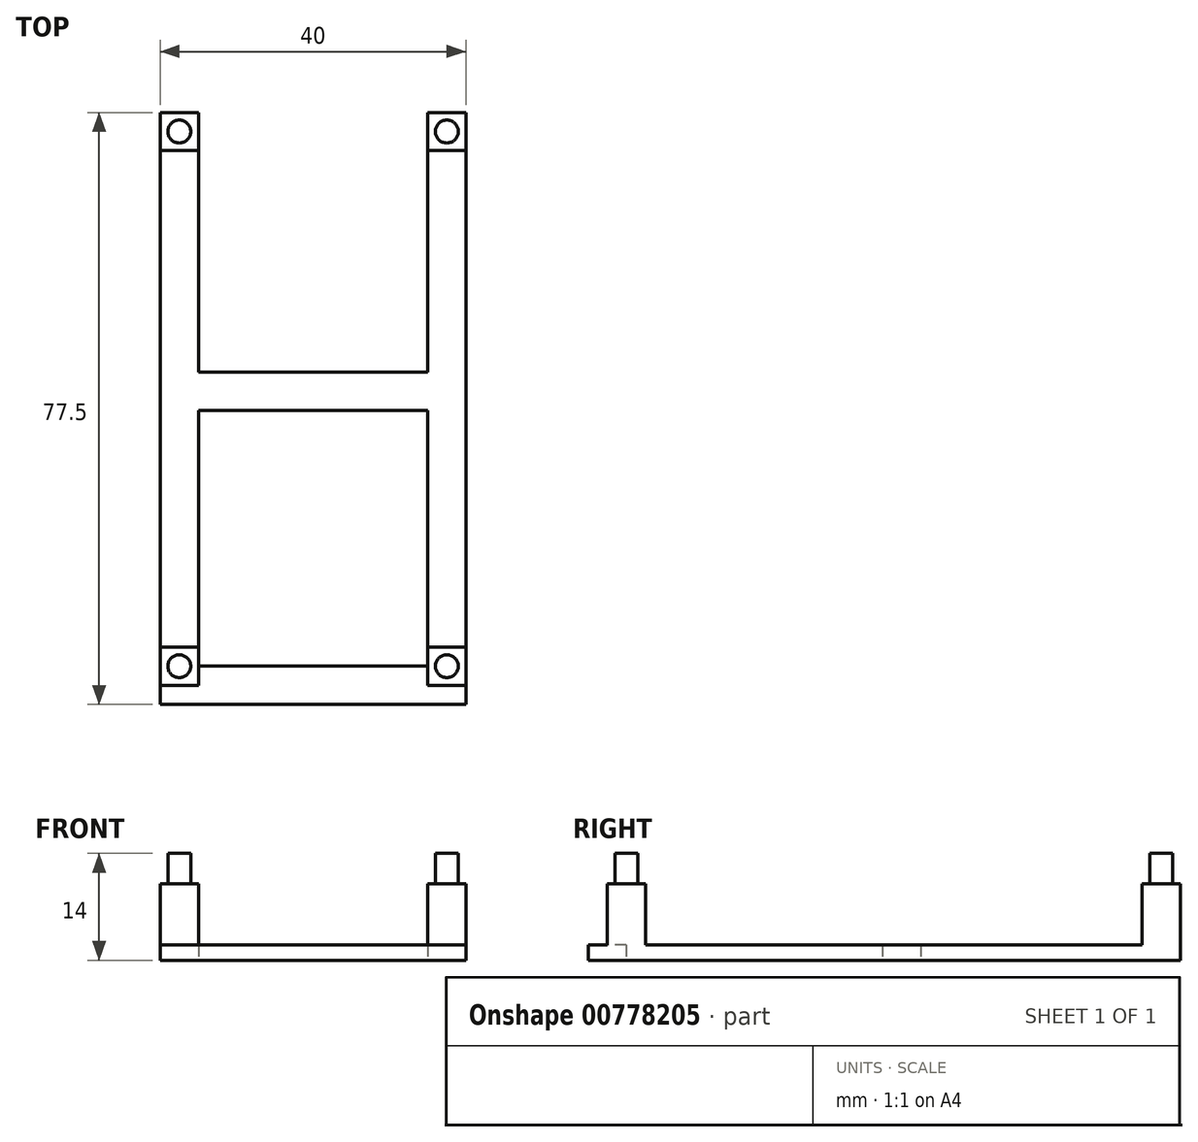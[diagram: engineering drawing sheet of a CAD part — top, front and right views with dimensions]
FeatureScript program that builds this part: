
annotation { "Feature Type Name" : "Feature", "Feature Type Description" : "" }
export const myFeature = defineFeature(function(context is Context, id is Id, definition is map)
    precondition{}
    {
        {
            var Q0;
            Q0=qCreatedBy(makeId("Top.planeOp"),FACE);
            var sketch = newSketch(context, id + "F0", { "sketchPlane" : qUnion([Q0])});
            skLineSegment(sketch, "E0.bottom", {"start": v(20, -41) * mm, "end": v(-20, -41) * mm});
            skLineSegment(sketch, "E0.top", {"start": v(20, 41) * mm, "end": v(-20, 41) * mm});
            skLineSegment(sketch, "E0.left", {"start": v(20, -41) * mm, "end": v(20, 41) * mm});
            skLineSegment(sketch, "E0.right", {"start": v(-20, -41) * mm, "end": v(-20, 41) * mm});
            skPoint(sketch, "E0.middle", {"position": v(0, 0) * mm});
            skLineSegment(sketch, "E1.bottom", {"start": v(-15, 31.5) * mm, "end": v(-20, 31.5) * mm});
            skLineSegment(sketch, "E1.top", {"start": v(-15, 36.5) * mm, "end": v(-20, 36.5) * mm});
            skLineSegment(sketch, "E1.left", {"start": v(-15, 31.5) * mm, "end": v(-15, 36.5) * mm});
            skLineSegment(sketch, "E1.right", {"start": v(-20, 31.5) * mm, "end": v(-20, 36.5) * mm});
            skPoint(sketch, "E1.middle", {"position": v(-17.5, 34) * mm});
            skCircle(sketch, "E2", {"center": v(-17.5, 34) * mm, "radius": 1.5 * mm});
            skLineSegment(sketch, "E3.bottom", {"start": v(20, 31.5) * mm, "end": v(15, 31.5) * mm});
            skLineSegment(sketch, "E3.top", {"start": v(20, 36.5) * mm, "end": v(15, 36.5) * mm});
            skLineSegment(sketch, "E3.left", {"start": v(20, 31.5) * mm, "end": v(20, 36.5) * mm});
            skLineSegment(sketch, "E3.right", {"start": v(15, 31.5) * mm, "end": v(15, 36.5) * mm});
            skPoint(sketch, "E3.middle", {"position": v(17.5, 34) * mm});
            skLineSegment(sketch, "E4.bottom", {"start": v(20, -38.5) * mm, "end": v(15, -38.5) * mm});
            skLineSegment(sketch, "E4.top", {"start": v(20, -33.5) * mm, "end": v(15, -33.5) * mm});
            skLineSegment(sketch, "E4.left", {"start": v(20, -38.5) * mm, "end": v(20, -33.5) * mm});
            skLineSegment(sketch, "E4.right", {"start": v(15, -38.5) * mm, "end": v(15, -33.5) * mm});
            skPoint(sketch, "E4.middle", {"position": v(17.5, -36) * mm});
            skLineSegment(sketch, "E5.bottom", {"start": v(-15, -38.5) * mm, "end": v(-20, -38.5) * mm});
            skLineSegment(sketch, "E5.top", {"start": v(-15, -33.5) * mm, "end": v(-20, -33.5) * mm});
            skLineSegment(sketch, "E5.left", {"start": v(-15, -38.5) * mm, "end": v(-15, -33.5) * mm});
            skLineSegment(sketch, "E5.right", {"start": v(-20, -38.5) * mm, "end": v(-20, -33.5) * mm});
            skPoint(sketch, "E5.middle", {"position": v(-17.5, -36) * mm});
            skCircle(sketch, "E6", {"center": v(17.5, 34) * mm, "radius": 1.5 * mm});
            skCircle(sketch, "E7", {"center": v(-17.5, -36) * mm, "radius": 1.5 * mm});
            skCircle(sketch, "E8", {"center": v(17.5, -36) * mm, "radius": 1.5 * mm});
            skLineSegment(sketch, "E9.bottom", {"start": v(-20, 31.5) * mm, "end": v(-15, 31.5) * mm});
            skLineSegment(sketch, "E9.top", {"start": v(-20, -33.5) * mm, "end": v(-15, -33.5) * mm});
            skLineSegment(sketch, "E9.left", {"start": v(-20, 31.5) * mm, "end": v(-20, -33.5) * mm});
            skLineSegment(sketch, "E9.right", {"start": v(-15, 31.5) * mm, "end": v(-15, -33.5) * mm});
            skLineSegment(sketch, "E10.left", {"start": v(20, 31.5) * mm, "end": v(20, -33.5) * mm});
            skLineSegment(sketch, "E10.right", {"start": v(15, 31.5) * mm, "end": v(15, -33.5) * mm});
            skLineSegment(sketch, "E11.bottom", {"start": v(-15, 31.5) * mm, "end": v(15, 31.5) * mm});
            skLineSegment(sketch, "E11.top", {"start": v(-15, 36.5) * mm, "end": v(15, 36.5) * mm});
            skLineSegment(sketch, "E12.bottom", {"start": v(-15, -33.5) * mm, "end": v(15, -33.5) * mm});
            skLineSegment(sketch, "E12.top", {"start": v(-15, -38.5) * mm, "end": v(15, -38.5) * mm});
            skLineSegment(sketch, "E12.left", {"start": v(-15, -33.5) * mm, "end": v(-15, -38.5) * mm});
            skLineSegment(sketch, "E12.right", {"start": v(15, -33.5) * mm, "end": v(15, -38.5) * mm});
            skLineSegment(sketch, "E13.bottom", {"start": v(20, 2.5) * mm, "end": v(-20, 2.5) * mm});
            skLineSegment(sketch, "E13.top", {"start": v(20, -2.5) * mm, "end": v(-20, -2.5) * mm});
            skLineSegment(sketch, "E13.left", {"start": v(20, 2.5) * mm, "end": v(20, -2.5) * mm});
            skLineSegment(sketch, "E13.right", {"start": v(-20, 2.5) * mm, "end": v(-20, -2.5) * mm});
            skLineSegment(sketch, "E14.bottom", {"start": v(-15, -36) * mm, "end": v(15, -36) * mm});
            skLineSegment(sketch, "E14.left", {"start": v(-15, -36) * mm, "end": v(-15, -38.5) * mm});
            skLineSegment(sketch, "E14.right", {"start": v(15, -36) * mm, "end": v(15, -38.5) * mm});
            skSolve(sketch);
        }
        {
            var Q0;
            {var subQ2=sQuery(id+"F0.wireOp",EDGE,"E0.bottom");Q0=makeQuery(id+"F0.imprint","IMPRINT",FACE,{"disambiguationData":[TD([[makeQuery(id+"F0.imprint","IMPRINT",EDGE,{"derivedFrom":subQ2}),-1.0]])]});}
            var Q1;
            {var subQ0=sQuery(id+"F0.wireOp",EDGE,"E1.bottom");Q1=makeQuery(id+"F0.imprint","IMPRINT",FACE,{"disambiguationData":[TD([[makeQuery(id+"F0.imprint","IMPRINT",EDGE,{"derivedFrom":subQ0}),1.0]])]});}
            var Q2;
            {var subQ0=sQuery(id+"F0.wireOp",EDGE,"E5.top");Q2=makeQuery(id+"F0.imprint","IMPRINT",FACE,{"disambiguationData":[TD([[makeQuery(id+"F0.imprint","IMPRINT",EDGE,{"derivedFrom":subQ0}),-1.0]])]});}
            var Q3;
            {var subQ0=sQuery(id+"F0.wireOp",EDGE,"E13.bottom");var subQ1=sQuery(id+"F0.wireOp",EDGE,"E0.right");var subQ2=makeQuery(id+"F0.imprint","INTERSECT",VERTEX,{"derivedFrom":[subQ1,subQ0]});Q3=makeQuery(id+"F0.imprint","IMPRINT",FACE,{"disambiguationData":[TD([[makeQuery(id+"F0.imprint","IMPRINT",EDGE,{"disambiguationData":[TD([[subQ2,1.0]])],"derivedFrom":subQ1}),-1.0]])]});}
            var Q4;
            {var subQ0=sQuery(id+"F0.wireOp",EDGE,"E3.bottom");Q4=makeQuery(id+"F0.imprint","IMPRINT",FACE,{"disambiguationData":[TD([[makeQuery(id+"F0.imprint","IMPRINT",EDGE,{"derivedFrom":subQ0}),1.0]])]});}
            var Q5;
            {var subQ0=sQuery(id+"F0.wireOp",EDGE,"E4.top");Q5=makeQuery(id+"F0.imprint","IMPRINT",FACE,{"disambiguationData":[TD([[makeQuery(id+"F0.imprint","IMPRINT",EDGE,{"derivedFrom":subQ0}),-1.0]])]});}
            var Q6;
            {var subQ0=sQuery(id+"F0.wireOp",EDGE,"E13.top");var subQ1=sQuery(id+"F0.wireOp",EDGE,"E0.left");var subQ2=makeQuery(id+"F0.imprint","INTERSECT",VERTEX,{"derivedFrom":[subQ1,subQ0]});Q6=makeQuery(id+"F0.imprint","IMPRINT",FACE,{"disambiguationData":[TD([[makeQuery(id+"F0.imprint","IMPRINT",EDGE,{"disambiguationData":[TD([[subQ2,-1.0]])],"derivedFrom":subQ1}),1.0]])]});}
            var Q7;
            {var subQ1=sQuery(id+"F0.wireOp",EDGE,"E1.bottom");Q7=makeQuery(id+"F0.imprint","IMPRINT",FACE,{"disambiguationData":[TD([[makeQuery(id+"F0.imprint","IMPRINT",EDGE,{"derivedFrom":subQ1}),-1.0]])]});}
            var Q8;
            {var subQ1=sQuery(id+"F0.wireOp",EDGE,"E3.bottom");Q8=makeQuery(id+"F0.imprint","IMPRINT",FACE,{"disambiguationData":[TD([[makeQuery(id+"F0.imprint","IMPRINT",EDGE,{"derivedFrom":subQ1}),-1.0]])]});}
            var Q9;
            {var subQ3=sQuery(id+"F0.wireOp",EDGE,"E4.bottom");Q9=makeQuery(id+"F0.imprint","IMPRINT",FACE,{"disambiguationData":[TD([[makeQuery(id+"F0.imprint","IMPRINT",EDGE,{"derivedFrom":subQ3}),-1.0]])]});}
            var Q10;
            {var subQ1=sQuery(id+"F0.wireOp",EDGE,"E5.bottom");Q10=makeQuery(id+"F0.imprint","IMPRINT",FACE,{"disambiguationData":[TD([[makeQuery(id+"F0.imprint","IMPRINT",EDGE,{"derivedFrom":subQ1}),-1.0]])]});}
            var Q11;
            Q11=makeQuery(id+"F0.imprint","IMPRINT",FACE,{"disambiguationData":[TD([[makeQuery(id+"F0.imprint","IMPRINT",EDGE,{"derivedFrom":sQuery(id+"F0.wireOp",EDGE,"E2")}),1.0]])]});
            var Q12;
            Q12=makeQuery(id+"F0.imprint","IMPRINT",FACE,{"disambiguationData":[TD([[makeQuery(id+"F0.imprint","IMPRINT",EDGE,{"derivedFrom":sQuery(id+"F0.wireOp",EDGE,"E6")}),1.0]])]});
            var Q13;
            {var subQ0=sQuery(id+"F0.wireOp",EDGE,"E13.top");var subQ1=sQuery(id+"F0.wireOp",EDGE,"E9.right");var subQ2=makeQuery(id+"F0.imprint","INTERSECT",VERTEX,{"derivedFrom":[subQ1,subQ0]});Q13=makeQuery(id+"F0.imprint","IMPRINT",FACE,{"disambiguationData":[TD([[makeQuery(id+"F0.imprint","IMPRINT",EDGE,{"disambiguationData":[TD([[subQ2,1.0]])],"derivedFrom":subQ1}),1.0]])]});}
            var Q14;
            Q14=makeQuery(id+"F0.imprint","IMPRINT",FACE,{"disambiguationData":[TD([[makeQuery(id+"F0.imprint","IMPRINT",EDGE,{"derivedFrom":sQuery(id+"F0.wireOp",EDGE,"E7")}),1.0]])]});
            var Q15;
            Q15=makeQuery(id+"F0.imprint","IMPRINT",FACE,{"disambiguationData":[TD([[makeQuery(id+"F0.imprint","IMPRINT",EDGE,{"derivedFrom":sQuery(id+"F0.wireOp",EDGE,"E8")}),1.0]])]});
            var Q16;
            {var subQ0=sQuery(id+"F0.wireOp",EDGE,"E12.top");Q16=makeQuery(id+"F0.imprint","IMPRINT",FACE,{"disambiguationData":[TD([[makeQuery(id+"F0.imprint","IMPRINT",EDGE,{"derivedFrom":subQ0}),1.0]])]});}
            extrude(context, id + "F1", {"entities" : qUnion([Q0, Q1, Q2, Q3, Q4, Q5, Q6, Q7, Q8, Q9, Q10, Q11, Q12, Q13, Q14, Q15, Q16]), "depth" : 2 * mm, "offsetDistance" : 25 * mm});
        }
        {
            var Q0;
            {var subQ1=sQuery(id+"F0.wireOp",EDGE,"E3.bottom");Q0=makeQuery(id+"F0.imprint","IMPRINT",FACE,{"disambiguationData":[TD([[makeQuery(id+"F0.imprint","IMPRINT",EDGE,{"derivedFrom":subQ1}),-1.0]])]});}
            var Q1;
            Q1=makeQuery(id+"F0.imprint","IMPRINT",FACE,{"disambiguationData":[TD([[makeQuery(id+"F0.imprint","IMPRINT",EDGE,{"derivedFrom":sQuery(id+"F0.wireOp",EDGE,"E6")}),1.0]])]});
            var Q2;
            {var subQ1=sQuery(id+"F0.wireOp",EDGE,"E1.bottom");Q2=makeQuery(id+"F0.imprint","IMPRINT",FACE,{"disambiguationData":[TD([[makeQuery(id+"F0.imprint","IMPRINT",EDGE,{"derivedFrom":subQ1}),-1.0]])]});}
            var Q3;
            Q3=makeQuery(id+"F0.imprint","IMPRINT",FACE,{"disambiguationData":[TD([[makeQuery(id+"F0.imprint","IMPRINT",EDGE,{"derivedFrom":sQuery(id+"F0.wireOp",EDGE,"E2")}),1.0]])]});
            var Q4;
            {var subQ3=sQuery(id+"F0.wireOp",EDGE,"E4.bottom");Q4=makeQuery(id+"F0.imprint","IMPRINT",FACE,{"disambiguationData":[TD([[makeQuery(id+"F0.imprint","IMPRINT",EDGE,{"derivedFrom":subQ3}),-1.0]])]});}
            var Q5;
            Q5=makeQuery(id+"F0.imprint","IMPRINT",FACE,{"disambiguationData":[TD([[makeQuery(id+"F0.imprint","IMPRINT",EDGE,{"derivedFrom":sQuery(id+"F0.wireOp",EDGE,"E8")}),1.0]])]});
            var Q6;
            {var subQ1=sQuery(id+"F0.wireOp",EDGE,"E5.bottom");Q6=makeQuery(id+"F0.imprint","IMPRINT",FACE,{"disambiguationData":[TD([[makeQuery(id+"F0.imprint","IMPRINT",EDGE,{"derivedFrom":subQ1}),-1.0]])]});}
            var Q7;
            Q7=makeQuery(id+"F0.imprint","IMPRINT",FACE,{"disambiguationData":[TD([[makeQuery(id+"F0.imprint","IMPRINT",EDGE,{"derivedFrom":sQuery(id+"F0.wireOp",EDGE,"E7")}),1.0]])]});
            extrude(context, id + "F2", {"entities" : qUnion([Q0, Q1, Q2, Q3, Q4, Q5, Q6, Q7]), "operationType" : NewBodyOperationType.ADD, "depth" : 10 * mm, "offsetDistance" : 25 * mm});
        }
        {
            var Q0;
            Q0=makeQuery(id+"F0.imprint","IMPRINT",FACE,{"disambiguationData":[TD([[makeQuery(id+"F0.imprint","IMPRINT",EDGE,{"derivedFrom":sQuery(id+"F0.wireOp",EDGE,"E6")}),1.0]])]});
            var Q1;
            Q1=makeQuery(id+"F0.imprint","IMPRINT",FACE,{"disambiguationData":[TD([[makeQuery(id+"F0.imprint","IMPRINT",EDGE,{"derivedFrom":sQuery(id+"F0.wireOp",EDGE,"E2")}),1.0]])]});
            var Q2;
            Q2=makeQuery(id+"F0.imprint","IMPRINT",FACE,{"disambiguationData":[TD([[makeQuery(id+"F0.imprint","IMPRINT",EDGE,{"derivedFrom":sQuery(id+"F0.wireOp",EDGE,"E8")}),1.0]])]});
            var Q3;
            Q3=makeQuery(id+"F0.imprint","IMPRINT",FACE,{"disambiguationData":[TD([[makeQuery(id+"F0.imprint","IMPRINT",EDGE,{"derivedFrom":sQuery(id+"F0.wireOp",EDGE,"E7")}),1.0]])]});
            extrude(context, id + "F3", {"entities" : qUnion([Q0, Q1, Q2, Q3]), "operationType" : NewBodyOperationType.ADD, "depth" : 14 * mm, "offsetDistance" : 25 * mm});
        }
    });
